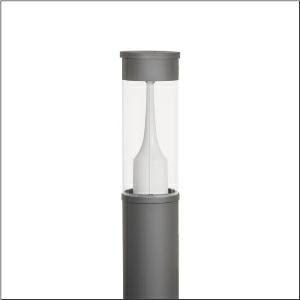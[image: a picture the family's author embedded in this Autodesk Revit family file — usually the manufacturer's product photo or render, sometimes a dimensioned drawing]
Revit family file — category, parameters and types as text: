
# Revit family: city-light_260_iq___p1_0a_5xa5295bf14h_d7c3
name_source: partatom
category: Lighting Fixtures
units: mm (PartAtom-declared; Revit-internal decimal feet)

## family parameters
Cut with Voids When Loaded = No
Host = Face
Light Source = No
Part Type = Normal
Room Calculation Point = No
Round Connector Dimension = Use Diameter
Shared = No

## types (1)
- --- (1 x LED, 1510 lm, 12.9 W, 2200K)
    Apparent Load = 13 VA
    CIE Flux Codes = 32 61 90 93 100
    Color Rendering = 70
    Color Temperature = 2200K
    Default Elevation = 1800 mm
    Description = City-Light 260 iQ, light pillar, Module 540 iQ-SR, primary light control with 3 zone facetted reflector, of plastic, silver coated, highly specular, structured, primary optical cover: cover, of PMMA, transparent, partly coated, light distribution: P1.0a, primary light characteristic: strongly asymmetric, LED, High Power LED, rated luminous flux: 1.510lm, luminous efficacy: 117lm/W, light colour: 722, colour temperature: 2200K, control gear: ECG iQ, control: presetting dimming logarithmic, Street-Remote, Auto-Match, Temp-Guard, Lumen-Switch, Night-Set, Smart-Wire, Light-Fading, Desk-Remote (wireless, voltage-free reading and setting of iQ features in the workshop via application-optimized NFC function/RFID function), optimised constant luminous flux control (CLO 2.0), with terminal, 6-pole, max. 2.5mm², mains connection: 230..240V, AC, 50/60Hz, start of lifetime: 13W, end of service life: 13W, reduction: 6W, luminaire housing, cylindrical, of extruded aluminium section, coated, Siteco® metallic grey (DB 702S), length: 2.600mm, diameter: 200mm, Module 540 iQ-SR, traffic white (RAL 9016), equipment: standard, protection rating (complete): IP65, insulation class (complete): insulation class II (safety insulation), certification: CE, ENEC, VDE, packaging unit: 1 piece

Light Distribution: P1.0a
    Height = 500 mm
    Lamp = 1 x LED
    Lamp Light Flux = 1510 lm
    Lamp Power = 12.9 W
    Lamp count = 1
    Length = 200 mm  [stored 0.656168 ft]
    Luminous efficacy = 117 lm/W
    Manufacturer = Siteco
    ModVariant = No
    Model = 5XA5295BF14H
    Mounting Place = Floor
    Mounting Type = Freestanding
    Number of Poles = 1
    OnlyDefault = Yes
    Power Factor = 1
    Product Name = City-Light 260 iQ | P1.0a
    Product group = light pillar
    ProductGroupID = 1303
    Protection Class = Protection class II
    Protection Degree = IP 65
    RLX_Detail_Level = 1
    RLX_Emergency_Light_Flux = 0 lm
    RLX_Emergency_Type = 0
    RLX_Emergency_Type_DB = No
    RlxData = <blob elided: 52949 chars, md5=becf7087>
    Socket = socket
    Standby Power = 0 W
    System Light Flux = 1510 lm
    System Power = 13 W
    Type Comments = factory setting: luminous flux: 100 % | dim-lin: 254 | 516 mA
    Type Image = l_1006918.jpg
    URL = http://relux.com
    VarID = @adj_091853
    Voltage = 0 V
    Weight = 0.00 kg
    Width = 0 mm  [stored 0 ft]

note: [stored X ft] marks values corroborated as IEEE doubles in the binary element streams (Revit-internal decimal feet)

## geometry (parser evidence)
native form markers: Blend x4, Sweep x12
no freeform markers — native parametric forms only
